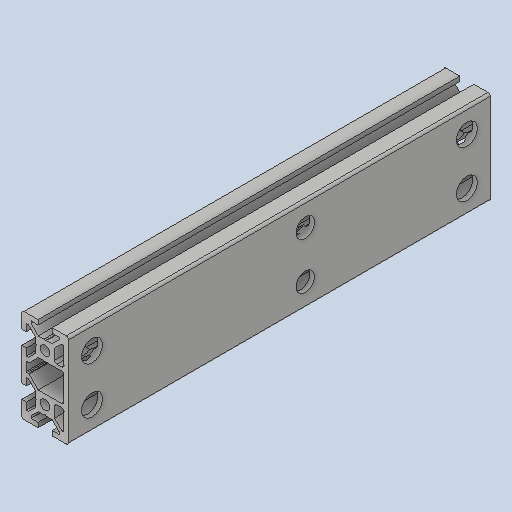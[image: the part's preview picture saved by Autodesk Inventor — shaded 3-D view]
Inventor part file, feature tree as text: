
AUTODESK INVENTOR PART (.ipt)
format: ipt  version: 2022 (Build 260153000, 153)  size: 453,632 bytes
history: native  units: mm
features: sketch x8, hole x7, other x7, extrude x1, pattern_linear x1
ambient origin geometry x8: Origin, YZ Plane, XZ Plane, XY Plane, X Axis, Y Axis, Z Axis, Center Point
bodies: Solid1 (feature_tree)
feature tree (24):
  extrude  "Extrusion1"  Depth=10.0mm TaperAngle=0.0deg
  hole  "Hole1"  [1 undecoded]
  pattern_linear  "Rectangular Pattern1"  Spacing1=101.0mm  [1 undecoded]
  hole  "Hole2"  [1 undecoded]
  hole  "Hole3"  [1 undecoded]
  hole  "Hole4"  [1 undecoded]
  hole  "Hole5"  [1 undecoded]
  other  "C1_XY"
  other  "C1_YZ"
  other  "C1_ZX"
  other  "C1_X"
  other  "C1_Y"
  other  "C1_Z"
  other  "C1_Center"
  hole  "穴8"  [1 undecoded]
  hole  "穴9"  [1 undecoded]
  sketch  "Sketch_63"  dims[d36=7.1mm d37=6.0mm d38=4.0mm d39=2.0mm d40=90.0deg d41=20.0mm d42=0.0mm d43=0.0mm d67=9.0mm d68=6.0mm d69=4.0mm d70=2.0mm d71=90.0deg d72=3.0mm d73=20.594885mm d74=101.0mm d75=101.0mm d76=6.0mm d77=6.0mm d78=8.0mm d79=4.0mm d80=90.0deg d81=8.0mm d82=20.594885mm]
  sketch  "Sketch2"  dims[d0=180.0mm d1=0.0mm]
  sketch  "Sketch3"  dims[d2=4.2mm d3=6.0mm d4=4.0mm d5=2.0mm d6=90.0deg d7=180.0mm d8=0.0mm d9=20.0mm d11=20.0mm d12=10.0mm d14=0.0mm]
  sketch  "Sketch4"  dims[d15=7.1mm d16=6.0mm d17=4.0mm d18=2.0mm d19=90.0deg d20=20.0mm d21=0.0mm]
  sketch  "Sketch5"  dims[d22=7.1mm d23=6.0mm d24=4.0mm d25=2.0mm d26=90.0deg d27=20.0mm d28=0.0mm]
  sketch  "Sketch6"  dims[d29=7.1mm d30=6.0mm d31=4.0mm d32=2.0mm d33=90.0deg d34=20.0mm d35=0.0mm]
  sketch  "スケッチ9"
  sketch  "スケッチ11"
note: 8 required parameter values undecoded (feature->parameter linkage not recoverable at this tier; creation-order binding heuristic only, values carry confidence <= 0.55)
